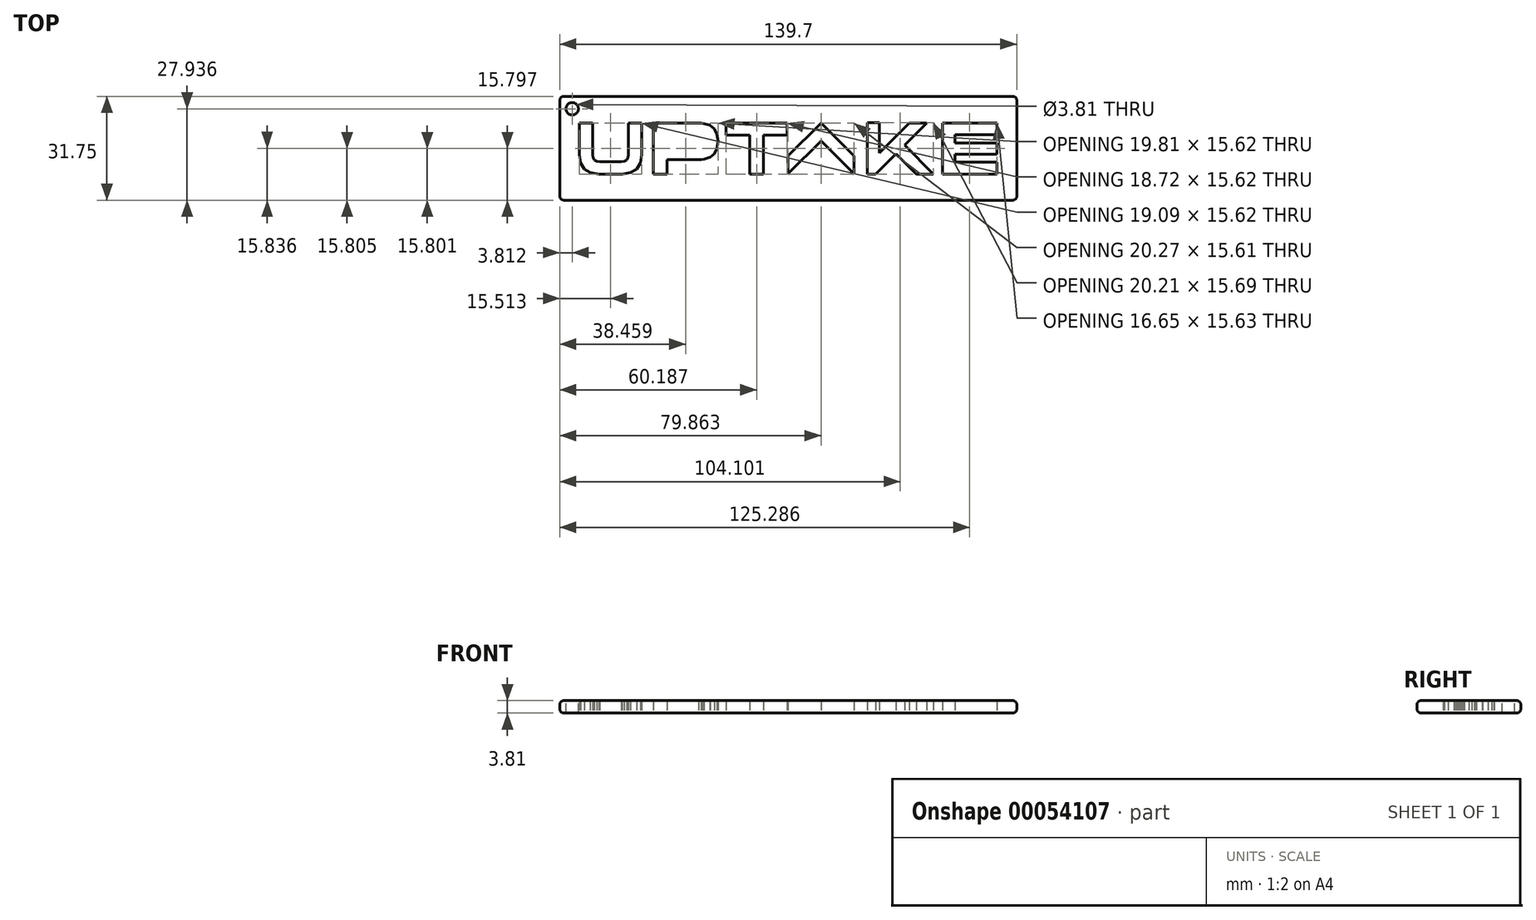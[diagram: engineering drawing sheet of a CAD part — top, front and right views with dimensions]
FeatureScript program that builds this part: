
annotation { "Feature Type Name" : "Feature", "Feature Type Description" : "" }
export const myFeature = defineFeature(function(context is Context, id is Id, definition is map)
    precondition{}
    {
        {
            var Q0;
            Q0=qCreatedBy(makeId("Top.planeOp"),FACE);
            var sketch = newSketch(context, id + "F0", { "sketchPlane" : qUnion([Q0])});
            skLineSegment(sketch, "E0", {"start": v(-25.67, 1.94) * mm, "end": v(-25.78, 1.11) * mm});
            skLineSegment(sketch, "E1", {"start": v(-25.78, 1.11) * mm, "end": v(-26.12, 0.53) * mm});
            skLineSegment(sketch, "E2", {"start": v(-26.12, 0.53) * mm, "end": v(-26.68, 0.18) * mm});
            skLineSegment(sketch, "E3", {"start": v(-26.68, 0.18) * mm, "end": v(-27.43, 0.05) * mm});
            skLineSegment(sketch, "E4", {"start": v(-27.43, 0.05) * mm, "end": v(-37.24, 0.05) * mm});
            skLineSegment(sketch, "E5", {"start": v(-37.24, 0.05) * mm, "end": v(-37.24, 4) * mm});
            skLineSegment(sketch, "E6", {"start": v(-37.24, 4) * mm, "end": v(-27.43, 4) * mm});
            skLineSegment(sketch, "E7", {"start": v(-27.43, 4) * mm, "end": v(-26.68, 3.88) * mm});
            skLineSegment(sketch, "E8", {"start": v(-26.68, 3.88) * mm, "end": v(-26.12, 3.53) * mm});
            skLineSegment(sketch, "E9", {"start": v(-26.12, 3.53) * mm, "end": v(-25.78, 2.94) * mm});
            skLineSegment(sketch, "E10", {"start": v(-25.78, 2.94) * mm, "end": v(-25.67, 2.12) * mm});
            skLineSegment(sketch, "E11", {"start": v(-25.67, 2.12) * mm, "end": v(-25.67, 1.94) * mm});
            skLineSegment(sketch, "E12", {"start": v(-26.08, 7.62) * mm, "end": v(-26.8, 7.7) * mm});
            skLineSegment(sketch, "E13", {"start": v(-26.8, 7.7) * mm, "end": v(-27.55, 7.73) * mm});
            skLineSegment(sketch, "E14", {"start": v(-27.55, 7.73) * mm, "end": v(-41.43, 7.73) * mm});
            skLineSegment(sketch, "E15", {"start": v(-41.43, 7.73) * mm, "end": v(-41.43, -7.9) * mm});
            skLineSegment(sketch, "E16", {"start": v(-41.43, -7.9) * mm, "end": v(-37.24, -7.9) * mm});
            skLineSegment(sketch, "E17", {"start": v(-37.24, -7.9) * mm, "end": v(-37.24, -3.54) * mm});
            skLineSegment(sketch, "E18", {"start": v(-37.24, -3.54) * mm, "end": v(-27.55, -3.54) * mm});
            skLineSegment(sketch, "E19", {"start": v(-27.55, -3.54) * mm, "end": v(-26.6, -3.5) * mm});
            skLineSegment(sketch, "E20", {"start": v(-26.6, -3.5) * mm, "end": v(-25.85, -3.4) * mm});
            skLineSegment(sketch, "E21", {"start": v(-25.85, -3.4) * mm, "end": v(-24.03, -2.78) * mm});
            skLineSegment(sketch, "E22", {"start": v(-24.03, -2.78) * mm, "end": v(-22.7, -1.66) * mm});
            skLineSegment(sketch, "E23", {"start": v(-22.7, -1.66) * mm, "end": v(-21.9, -0.03) * mm});
            skLineSegment(sketch, "E24", {"start": v(-21.9, -0.03) * mm, "end": v(-21.61, 2.07) * mm});
            skLineSegment(sketch, "E25", {"start": v(-21.61, 2.07) * mm, "end": v(-21.9, 4.23) * mm});
            skLineSegment(sketch, "E26", {"start": v(-21.9, 4.23) * mm, "end": v(-22.76, 5.9) * mm});
            skLineSegment(sketch, "E27", {"start": v(-22.76, 5.9) * mm, "end": v(-24.16, 7.03) * mm});
            skLineSegment(sketch, "E28", {"start": v(-24.16, 7.03) * mm, "end": v(-26.08, 7.62) * mm});
            skLineSegment(sketch, "E29", {"start": v(63.63, -7.9) * mm, "end": v(46.98, -7.9) * mm});
            skLineSegment(sketch, "E30", {"start": v(46.98, -7.9) * mm, "end": v(46.98, 7.73) * mm});
            skLineSegment(sketch, "E31", {"start": v(46.98, 7.73) * mm, "end": v(63.63, 7.73) * mm});
            skLineSegment(sketch, "E32", {"start": v(63.63, 7.73) * mm, "end": v(63.63, 4.11) * mm});
            skLineSegment(sketch, "E33", {"start": v(63.63, 4.11) * mm, "end": v(50.79, 4.11) * mm});
            skLineSegment(sketch, "E34", {"start": v(50.79, 4.11) * mm, "end": v(50.79, 1.6) * mm});
            skLineSegment(sketch, "E35", {"start": v(50.79, 1.6) * mm, "end": v(63.63, 1.6) * mm});
            skLineSegment(sketch, "E36", {"start": v(63.63, 1.6) * mm, "end": v(63.63, -1.8) * mm});
            skLineSegment(sketch, "E37", {"start": v(63.63, -1.8) * mm, "end": v(50.79, -1.8) * mm});
            skLineSegment(sketch, "E38", {"start": v(50.79, -1.8) * mm, "end": v(50.79, -4.28) * mm});
            skLineSegment(sketch, "E39", {"start": v(50.79, -4.28) * mm, "end": v(63.63, -4.28) * mm});
            skLineSegment(sketch, "E40", {"start": v(63.63, -4.28) * mm, "end": v(63.63, -7.9) * mm});
            skLineSegment(sketch, "E41", {"start": v(-11.89, -7.9) * mm, "end": v(-7.7, -7.9) * mm});
            skLineSegment(sketch, "E42", {"start": v(-7.7, -7.9) * mm, "end": v(-7.7, 4) * mm});
            skLineSegment(sketch, "E43", {"start": v(-7.7, 4) * mm, "end": v(-0.43, 4) * mm});
            skLineSegment(sketch, "E44", {"start": v(-0.43, 4) * mm, "end": v(-0.43, 7.73) * mm});
            skLineSegment(sketch, "E45", {"start": v(-0.43, 7.73) * mm, "end": v(-19.15, 7.73) * mm});
            skLineSegment(sketch, "E46", {"start": v(-19.15, 7.73) * mm, "end": v(-19.15, 4) * mm});
            skLineSegment(sketch, "E47", {"start": v(-19.15, 4) * mm, "end": v(-11.89, 4) * mm});
            skLineSegment(sketch, "E48", {"start": v(-11.89, 4) * mm, "end": v(-11.89, -7.9) * mm});
            skLineSegment(sketch, "E49", {"start": v(-58.08, -7.9) * mm, "end": v(-50.86, -7.9) * mm});
            skLineSegment(sketch, "E50", {"start": v(-50.86, -7.9) * mm, "end": v(-48.31, -7.49) * mm});
            skLineSegment(sketch, "E51", {"start": v(-48.31, -7.49) * mm, "end": v(-46.47, -6.35) * mm});
            skLineSegment(sketch, "E52", {"start": v(-46.47, -6.35) * mm, "end": v(-45.34, -4.5) * mm});
            skLineSegment(sketch, "E53", {"start": v(-45.34, -4.5) * mm, "end": v(-44.92, -1.95) * mm});
            skLineSegment(sketch, "E54", {"start": v(-44.92, -1.95) * mm, "end": v(-44.92, 7.73) * mm});
            skLineSegment(sketch, "E55", {"start": v(-44.92, 7.73) * mm, "end": v(-48.97, 7.73) * mm});
            skLineSegment(sketch, "E56", {"start": v(-48.97, 7.73) * mm, "end": v(-48.97, -1.95) * mm});
            skLineSegment(sketch, "E57", {"start": v(-48.97, -1.95) * mm, "end": v(-49.12, -2.88) * mm});
            skLineSegment(sketch, "E58", {"start": v(-49.12, -2.88) * mm, "end": v(-49.55, -3.56) * mm});
            skLineSegment(sketch, "E59", {"start": v(-49.55, -3.56) * mm, "end": v(-50.25, -3.99) * mm});
            skLineSegment(sketch, "E60", {"start": v(-50.25, -3.99) * mm, "end": v(-51.18, -4.16) * mm});
            skLineSegment(sketch, "E61", {"start": v(-51.18, -4.16) * mm, "end": v(-57.75, -4.16) * mm});
            skLineSegment(sketch, "E62", {"start": v(-57.75, -4.16) * mm, "end": v(-58.7, -3.98) * mm});
            skLineSegment(sketch, "E63", {"start": v(-58.7, -3.98) * mm, "end": v(-59.38, -3.57) * mm});
            skLineSegment(sketch, "E64", {"start": v(-59.38, -3.57) * mm, "end": v(-59.8, -2.9) * mm});
            skLineSegment(sketch, "E65", {"start": v(-59.8, -2.9) * mm, "end": v(-59.96, -1.95) * mm});
            skLineSegment(sketch, "E66", {"start": v(-59.96, -1.95) * mm, "end": v(-59.96, 7.73) * mm});
            skLineSegment(sketch, "E67", {"start": v(-59.96, 7.73) * mm, "end": v(-64.01, 7.73) * mm});
            skLineSegment(sketch, "E68", {"start": v(-64.01, 7.73) * mm, "end": v(-64.01, -1.95) * mm});
            skLineSegment(sketch, "E69", {"start": v(-64.01, -1.95) * mm, "end": v(-63.6, -4.5) * mm});
            skLineSegment(sketch, "E70", {"start": v(-63.6, -4.5) * mm, "end": v(-62.47, -6.35) * mm});
            skLineSegment(sketch, "E71", {"start": v(-62.47, -6.35) * mm, "end": v(-60.63, -7.49) * mm});
            skLineSegment(sketch, "E72", {"start": v(-60.63, -7.49) * mm, "end": v(-58.08, -7.9) * mm});
            skLineSegment(sketch, "E73", {"start": v(44.23, -7.9) * mm, "end": v(38.96, -7.9) * mm});
            skLineSegment(sketch, "E74", {"start": v(38.96, -7.9) * mm, "end": v(32.77, -1.7) * mm});
            skLineSegment(sketch, "E75", {"start": v(32.77, -1.7) * mm, "end": v(26.58, -7.9) * mm});
            skLineSegment(sketch, "E76", {"start": v(26.58, -7.9) * mm, "end": v(24.02, -7.9) * mm});
            skLineSegment(sketch, "E77", {"start": v(24.02, -7.9) * mm, "end": v(24.02, 7.8) * mm});
            skLineSegment(sketch, "E78", {"start": v(24.02, 7.8) * mm, "end": v(27.76, 7.8) * mm});
            skLineSegment(sketch, "E79", {"start": v(27.76, 7.8) * mm, "end": v(27.76, -1.44) * mm});
            skLineSegment(sketch, "E80", {"start": v(27.76, -1.44) * mm, "end": v(36.9, 7.73) * mm});
            skLineSegment(sketch, "E81", {"start": v(36.9, 7.73) * mm, "end": v(42.2, 7.73) * mm});
            skLineSegment(sketch, "E82", {"start": v(42.2, 7.73) * mm, "end": v(35.4, 0.93) * mm});
            skLineSegment(sketch, "E83", {"start": v(35.4, 0.93) * mm, "end": v(44.23, -7.9) * mm});
            skLineSegment(sketch, "E84", {"start": v(19.96, -2.35) * mm, "end": v(10.02, 7.6) * mm});
            skLineSegment(sketch, "E85", {"start": v(10.02, 7.6) * mm, "end": v(9.88, 7.73) * mm});
            skLineSegment(sketch, "E86", {"start": v(9.88, 7.73) * mm, "end": v(9.75, 7.6) * mm});
            skLineSegment(sketch, "E87", {"start": v(9.75, 7.6) * mm, "end": v(-0.2, -2.35) * mm});
            skLineSegment(sketch, "E88", {"start": v(-0.2, -2.35) * mm, "end": v(-0.25, -2.4) * mm});
            skLineSegment(sketch, "E89", {"start": v(-0.25, -2.4) * mm, "end": v(-0.25, -2.48) * mm});
            skLineSegment(sketch, "E90", {"start": v(-0.25, -2.48) * mm, "end": v(-0.25, -7.43) * mm});
            skLineSegment(sketch, "E91", {"start": v(-0.25, -7.43) * mm, "end": v(-0.25, -7.88) * mm});
            skLineSegment(sketch, "E92", {"start": v(-0.25, -7.88) * mm, "end": v(0.06, -7.56) * mm});
            skLineSegment(sketch, "E93", {"start": v(0.06, -7.56) * mm, "end": v(9.88, 2.25) * mm});
            skLineSegment(sketch, "E94", {"start": v(9.88, 2.25) * mm, "end": v(19.7, -7.56) * mm});
            skLineSegment(sketch, "E95", {"start": v(19.7, -7.56) * mm, "end": v(20.02, -7.88) * mm});
            skLineSegment(sketch, "E96", {"start": v(20.02, -7.88) * mm, "end": v(20.02, -7.43) * mm});
            skLineSegment(sketch, "E97", {"start": v(20.02, -7.43) * mm, "end": v(20.02, -2.48) * mm});
            skLineSegment(sketch, "E98", {"start": v(20.02, -2.48) * mm, "end": v(20.02, -2.4) * mm});
            skLineSegment(sketch, "E99", {"start": v(20.02, -2.4) * mm, "end": v(19.96, -2.35) * mm});
            skLineSegment(sketch, "E100.bottom", {"start": v(-69.98, 15.87) * mm, "end": v(69.72, 15.87) * mm});
            skLineSegment(sketch, "E100.top", {"start": v(-69.98, -15.88) * mm, "end": v(69.72, -15.88) * mm});
            skLineSegment(sketch, "E100.left", {"start": v(-69.98, 15.87) * mm, "end": v(-69.98, -15.88) * mm});
            skLineSegment(sketch, "E100.right", {"start": v(69.72, 15.87) * mm, "end": v(69.72, -15.88) * mm});
            skSolve(sketch);
        }
        {
            var Q0;
            Q0=makeQuery(id+"F0.imprint","IMPRINT",FACE,{"disambiguationData":[TD([[makeQuery(id+"F0.imprint","IMPRINT",EDGE,{"derivedFrom":sQuery(id+"F0.wireOp",EDGE,"E12")}),-1.0]])]});
            extrude(context, id + "F1", {"entities" : qUnion([Q0]), "depth" : 3.8 * mm});
        }
        {
            var Q0;
            Q0=makeQuery(id+"F1.opExtrude","CAP_FACE",FACE,{"disambiguationData":[OSD([sQuery(id+"F0.wireOp",EDGE,"E12"),sQuery(id+"F0.wireOp",EDGE,"E13"),sQuery(id+"F0.wireOp",EDGE,"E14"),sQuery(id+"F0.wireOp",EDGE,"E15"),sQuery(id+"F0.wireOp",EDGE,"E16"),sQuery(id+"F0.wireOp",EDGE,"E17"),sQuery(id+"F0.wireOp",EDGE,"E18"),sQuery(id+"F0.wireOp",EDGE,"E19"),sQuery(id+"F0.wireOp",EDGE,"E20"),sQuery(id+"F0.wireOp",EDGE,"E21"),sQuery(id+"F0.wireOp",EDGE,"E22"),sQuery(id+"F0.wireOp",EDGE,"E23"),sQuery(id+"F0.wireOp",EDGE,"E24"),sQuery(id+"F0.wireOp",EDGE,"E25"),sQuery(id+"F0.wireOp",EDGE,"E26"),sQuery(id+"F0.wireOp",EDGE,"E27"),sQuery(id+"F0.wireOp",EDGE,"E28"),sQuery(id+"F0.wireOp",EDGE,"E29"),sQuery(id+"F0.wireOp",EDGE,"E30"),sQuery(id+"F0.wireOp",EDGE,"E31"),sQuery(id+"F0.wireOp",EDGE,"E32"),sQuery(id+"F0.wireOp",EDGE,"E33"),sQuery(id+"F0.wireOp",EDGE,"E34"),sQuery(id+"F0.wireOp",EDGE,"E35"),sQuery(id+"F0.wireOp",EDGE,"E36"),sQuery(id+"F0.wireOp",EDGE,"E37"),sQuery(id+"F0.wireOp",EDGE,"E38"),sQuery(id+"F0.wireOp",EDGE,"E39"),sQuery(id+"F0.wireOp",EDGE,"E40"),sQuery(id+"F0.wireOp",EDGE,"E41"),sQuery(id+"F0.wireOp",EDGE,"E42"),sQuery(id+"F0.wireOp",EDGE,"E43"),sQuery(id+"F0.wireOp",EDGE,"E44"),sQuery(id+"F0.wireOp",EDGE,"E45"),sQuery(id+"F0.wireOp",EDGE,"E46"),sQuery(id+"F0.wireOp",EDGE,"E47"),sQuery(id+"F0.wireOp",EDGE,"E48"),sQuery(id+"F0.wireOp",EDGE,"E49"),sQuery(id+"F0.wireOp",EDGE,"E50"),sQuery(id+"F0.wireOp",EDGE,"E51"),sQuery(id+"F0.wireOp",EDGE,"E52"),sQuery(id+"F0.wireOp",EDGE,"E53"),sQuery(id+"F0.wireOp",EDGE,"E54"),sQuery(id+"F0.wireOp",EDGE,"E55"),sQuery(id+"F0.wireOp",EDGE,"E56"),sQuery(id+"F0.wireOp",EDGE,"E57"),sQuery(id+"F0.wireOp",EDGE,"E58"),sQuery(id+"F0.wireOp",EDGE,"E59"),sQuery(id+"F0.wireOp",EDGE,"E60"),sQuery(id+"F0.wireOp",EDGE,"E61"),sQuery(id+"F0.wireOp",EDGE,"E62"),sQuery(id+"F0.wireOp",EDGE,"E63"),sQuery(id+"F0.wireOp",EDGE,"E64"),sQuery(id+"F0.wireOp",EDGE,"E65"),sQuery(id+"F0.wireOp",EDGE,"E66"),sQuery(id+"F0.wireOp",EDGE,"E67"),sQuery(id+"F0.wireOp",EDGE,"E68"),sQuery(id+"F0.wireOp",EDGE,"E69"),sQuery(id+"F0.wireOp",EDGE,"E70"),sQuery(id+"F0.wireOp",EDGE,"E71"),sQuery(id+"F0.wireOp",EDGE,"E72"),sQuery(id+"F0.wireOp",EDGE,"E73"),sQuery(id+"F0.wireOp",EDGE,"E74"),sQuery(id+"F0.wireOp",EDGE,"E75"),sQuery(id+"F0.wireOp",EDGE,"E76"),sQuery(id+"F0.wireOp",EDGE,"E77"),sQuery(id+"F0.wireOp",EDGE,"E78"),sQuery(id+"F0.wireOp",EDGE,"E79"),sQuery(id+"F0.wireOp",EDGE,"E80"),sQuery(id+"F0.wireOp",EDGE,"E81"),sQuery(id+"F0.wireOp",EDGE,"E82"),sQuery(id+"F0.wireOp",EDGE,"E83"),sQuery(id+"F0.wireOp",EDGE,"E84"),sQuery(id+"F0.wireOp",EDGE,"E85"),sQuery(id+"F0.wireOp",EDGE,"E86"),sQuery(id+"F0.wireOp",EDGE,"E87"),sQuery(id+"F0.wireOp",EDGE,"E88"),sQuery(id+"F0.wireOp",EDGE,"E89"),sQuery(id+"F0.wireOp",EDGE,"E90"),sQuery(id+"F0.wireOp",EDGE,"E91"),sQuery(id+"F0.wireOp",EDGE,"E92"),sQuery(id+"F0.wireOp",EDGE,"E93"),sQuery(id+"F0.wireOp",EDGE,"E94"),sQuery(id+"F0.wireOp",EDGE,"E95"),sQuery(id+"F0.wireOp",EDGE,"E96"),sQuery(id+"F0.wireOp",EDGE,"E97"),sQuery(id+"F0.wireOp",EDGE,"E98"),sQuery(id+"F0.wireOp",EDGE,"E99"),sQuery(id+"F0.wireOp",EDGE,"E100.bottom"),sQuery(id+"F0.wireOp",EDGE,"E100.top"),sQuery(id+"F0.wireOp",EDGE,"E100.left"),sQuery(id+"F0.wireOp",EDGE,"E100.right")])],"isStart":false});
            var sketch = newSketch(context, id + "F2", { "sketchPlane" : qUnion([Q0])});
            skPoint(sketch, "E101", {"position": v(-66.17, 12.06) * mm});
            skSolve(sketch);
        }
        {
            var Q0;
            Q0=sQuery(id+"F2.wireOp",VERTEX,"E101");
            var Q1;
            Q1=makeQuery(id+"F1.opExtrude","SWEPT_BODY",BODY,{"disambiguationData":[OSD([sQuery(id+"F0.wireOp",EDGE,"E12"),sQuery(id+"F0.wireOp",EDGE,"E13"),sQuery(id+"F0.wireOp",EDGE,"E14"),sQuery(id+"F0.wireOp",EDGE,"E15"),sQuery(id+"F0.wireOp",EDGE,"E16"),sQuery(id+"F0.wireOp",EDGE,"E17"),sQuery(id+"F0.wireOp",EDGE,"E18"),sQuery(id+"F0.wireOp",EDGE,"E19"),sQuery(id+"F0.wireOp",EDGE,"E20"),sQuery(id+"F0.wireOp",EDGE,"E21"),sQuery(id+"F0.wireOp",EDGE,"E22"),sQuery(id+"F0.wireOp",EDGE,"E23"),sQuery(id+"F0.wireOp",EDGE,"E24"),sQuery(id+"F0.wireOp",EDGE,"E25"),sQuery(id+"F0.wireOp",EDGE,"E26"),sQuery(id+"F0.wireOp",EDGE,"E27"),sQuery(id+"F0.wireOp",EDGE,"E28"),sQuery(id+"F0.wireOp",EDGE,"E29"),sQuery(id+"F0.wireOp",EDGE,"E30"),sQuery(id+"F0.wireOp",EDGE,"E31"),sQuery(id+"F0.wireOp",EDGE,"E32"),sQuery(id+"F0.wireOp",EDGE,"E33"),sQuery(id+"F0.wireOp",EDGE,"E34"),sQuery(id+"F0.wireOp",EDGE,"E35"),sQuery(id+"F0.wireOp",EDGE,"E36"),sQuery(id+"F0.wireOp",EDGE,"E37"),sQuery(id+"F0.wireOp",EDGE,"E38"),sQuery(id+"F0.wireOp",EDGE,"E39"),sQuery(id+"F0.wireOp",EDGE,"E40"),sQuery(id+"F0.wireOp",EDGE,"E41"),sQuery(id+"F0.wireOp",EDGE,"E42"),sQuery(id+"F0.wireOp",EDGE,"E43"),sQuery(id+"F0.wireOp",EDGE,"E44"),sQuery(id+"F0.wireOp",EDGE,"E45"),sQuery(id+"F0.wireOp",EDGE,"E46"),sQuery(id+"F0.wireOp",EDGE,"E47"),sQuery(id+"F0.wireOp",EDGE,"E48"),sQuery(id+"F0.wireOp",EDGE,"E49"),sQuery(id+"F0.wireOp",EDGE,"E50"),sQuery(id+"F0.wireOp",EDGE,"E51"),sQuery(id+"F0.wireOp",EDGE,"E52"),sQuery(id+"F0.wireOp",EDGE,"E53"),sQuery(id+"F0.wireOp",EDGE,"E54"),sQuery(id+"F0.wireOp",EDGE,"E55"),sQuery(id+"F0.wireOp",EDGE,"E56"),sQuery(id+"F0.wireOp",EDGE,"E57"),sQuery(id+"F0.wireOp",EDGE,"E58"),sQuery(id+"F0.wireOp",EDGE,"E59"),sQuery(id+"F0.wireOp",EDGE,"E60"),sQuery(id+"F0.wireOp",EDGE,"E61"),sQuery(id+"F0.wireOp",EDGE,"E62"),sQuery(id+"F0.wireOp",EDGE,"E63"),sQuery(id+"F0.wireOp",EDGE,"E64"),sQuery(id+"F0.wireOp",EDGE,"E65"),sQuery(id+"F0.wireOp",EDGE,"E66"),sQuery(id+"F0.wireOp",EDGE,"E67"),sQuery(id+"F0.wireOp",EDGE,"E68"),sQuery(id+"F0.wireOp",EDGE,"E69"),sQuery(id+"F0.wireOp",EDGE,"E70"),sQuery(id+"F0.wireOp",EDGE,"E71"),sQuery(id+"F0.wireOp",EDGE,"E72"),sQuery(id+"F0.wireOp",EDGE,"E73"),sQuery(id+"F0.wireOp",EDGE,"E74"),sQuery(id+"F0.wireOp",EDGE,"E75"),sQuery(id+"F0.wireOp",EDGE,"E76"),sQuery(id+"F0.wireOp",EDGE,"E77"),sQuery(id+"F0.wireOp",EDGE,"E78"),sQuery(id+"F0.wireOp",EDGE,"E79"),sQuery(id+"F0.wireOp",EDGE,"E80"),sQuery(id+"F0.wireOp",EDGE,"E81"),sQuery(id+"F0.wireOp",EDGE,"E82"),sQuery(id+"F0.wireOp",EDGE,"E83"),sQuery(id+"F0.wireOp",EDGE,"E84"),sQuery(id+"F0.wireOp",EDGE,"E85"),sQuery(id+"F0.wireOp",EDGE,"E86"),sQuery(id+"F0.wireOp",EDGE,"E87"),sQuery(id+"F0.wireOp",EDGE,"E88"),sQuery(id+"F0.wireOp",EDGE,"E89"),sQuery(id+"F0.wireOp",EDGE,"E90"),sQuery(id+"F0.wireOp",EDGE,"E91"),sQuery(id+"F0.wireOp",EDGE,"E92"),sQuery(id+"F0.wireOp",EDGE,"E93"),sQuery(id+"F0.wireOp",EDGE,"E94"),sQuery(id+"F0.wireOp",EDGE,"E95"),sQuery(id+"F0.wireOp",EDGE,"E96"),sQuery(id+"F0.wireOp",EDGE,"E97"),sQuery(id+"F0.wireOp",EDGE,"E98"),sQuery(id+"F0.wireOp",EDGE,"E99"),sQuery(id+"F0.wireOp",EDGE,"E100.bottom"),sQuery(id+"F0.wireOp",EDGE,"E100.top"),sQuery(id+"F0.wireOp",EDGE,"E100.left"),sQuery(id+"F0.wireOp",EDGE,"E100.right")])]});
            hole(context, id + "F3", {"style" : HoleStyle.SIMPLE, "holeDiameter" : 3.8 * mm, "endStyle" : HoleEndStyle.THROUGH, "locations" : qUnion([Q0]), "scope" : qUnion([Q1])});
        }
        {
            var Q0;
            Q0=makeQuery(id+"F1.opExtrude","CAP_EDGE",EDGE,{"disambiguationData":[OSD([sQuery(id+"F0.wireOp",EDGE,"E100.bottom")])],"isStart":false});
            var Q1;
            Q1=makeQuery(id+"F1.opExtrude","CAP_EDGE",EDGE,{"disambiguationData":[OSD([sQuery(id+"F0.wireOp",EDGE,"E100.left")])],"isStart":false});
            var Q2;
            Q2=makeQuery(id+"F1.opExtrude","CAP_EDGE",EDGE,{"disambiguationData":[OSD([sQuery(id+"F0.wireOp",EDGE,"E100.top")])],"isStart":false});
            var Q3;
            Q3=makeQuery(id+"F1.opExtrude","CAP_EDGE",EDGE,{"disambiguationData":[OSD([sQuery(id+"F0.wireOp",EDGE,"E100.right")])],"isStart":false});
            var Q4;
            Q4=makeQuery(id+"F1.opExtrude","CAP_EDGE",EDGE,{"disambiguationData":[OSD([sQuery(id+"F0.wireOp",EDGE,"E100.right")])],"isStart":true});
            var Q5;
            Q5=makeQuery(id+"F1.opExtrude","CAP_EDGE",EDGE,{"disambiguationData":[OSD([sQuery(id+"F0.wireOp",EDGE,"E100.bottom")])],"isStart":true});
            var Q6;
            Q6=makeQuery(id+"F1.opExtrude","CAP_EDGE",EDGE,{"disambiguationData":[OSD([sQuery(id+"F0.wireOp",EDGE,"E100.top")])],"isStart":true});
            var Q7;
            Q7=makeQuery(id+"F1.opExtrude","CAP_EDGE",EDGE,{"disambiguationData":[OSD([sQuery(id+"F0.wireOp",EDGE,"E100.left")])],"isStart":true});
            var Q8;
            Q8=makeQuery(id+"F3.hole-0.boolean.opBoolean","COPY",EDGE,{"derivedFrom":makeQuery(id+"F3.hole-0.opRevolve","SWEPT_EDGE",EDGE,{"disambiguationData":[OSD([sQuery(id+"F3.hole-0.sketch.wireOp",EDGE,"core_line_2"),sQuery(id+"F3.hole-0.sketch.wireOp",EDGE,"core_line_3")])]})});
            var Q9;
            Q9=makeQuery(id+"F3.hole-0.boolean.opBoolean","INTERSECT",EDGE,{"derivedFrom":[makeQuery(id+"F1.opExtrude","CAP_FACE",FACE,{"disambiguationData":[OSD([sQuery(id+"F0.wireOp",EDGE,"E12"),sQuery(id+"F0.wireOp",EDGE,"E13"),sQuery(id+"F0.wireOp",EDGE,"E14"),sQuery(id+"F0.wireOp",EDGE,"E15"),sQuery(id+"F0.wireOp",EDGE,"E16"),sQuery(id+"F0.wireOp",EDGE,"E17"),sQuery(id+"F0.wireOp",EDGE,"E18"),sQuery(id+"F0.wireOp",EDGE,"E19"),sQuery(id+"F0.wireOp",EDGE,"E20"),sQuery(id+"F0.wireOp",EDGE,"E21"),sQuery(id+"F0.wireOp",EDGE,"E22"),sQuery(id+"F0.wireOp",EDGE,"E23"),sQuery(id+"F0.wireOp",EDGE,"E24"),sQuery(id+"F0.wireOp",EDGE,"E25"),sQuery(id+"F0.wireOp",EDGE,"E26"),sQuery(id+"F0.wireOp",EDGE,"E27"),sQuery(id+"F0.wireOp",EDGE,"E28"),sQuery(id+"F0.wireOp",EDGE,"E29"),sQuery(id+"F0.wireOp",EDGE,"E30"),sQuery(id+"F0.wireOp",EDGE,"E31"),sQuery(id+"F0.wireOp",EDGE,"E32"),sQuery(id+"F0.wireOp",EDGE,"E33"),sQuery(id+"F0.wireOp",EDGE,"E34"),sQuery(id+"F0.wireOp",EDGE,"E35"),sQuery(id+"F0.wireOp",EDGE,"E36"),sQuery(id+"F0.wireOp",EDGE,"E37"),sQuery(id+"F0.wireOp",EDGE,"E38"),sQuery(id+"F0.wireOp",EDGE,"E39"),sQuery(id+"F0.wireOp",EDGE,"E40"),sQuery(id+"F0.wireOp",EDGE,"E41"),sQuery(id+"F0.wireOp",EDGE,"E42"),sQuery(id+"F0.wireOp",EDGE,"E43"),sQuery(id+"F0.wireOp",EDGE,"E44"),sQuery(id+"F0.wireOp",EDGE,"E45"),sQuery(id+"F0.wireOp",EDGE,"E46"),sQuery(id+"F0.wireOp",EDGE,"E47"),sQuery(id+"F0.wireOp",EDGE,"E48"),sQuery(id+"F0.wireOp",EDGE,"E49"),sQuery(id+"F0.wireOp",EDGE,"E50"),sQuery(id+"F0.wireOp",EDGE,"E51"),sQuery(id+"F0.wireOp",EDGE,"E52"),sQuery(id+"F0.wireOp",EDGE,"E53"),sQuery(id+"F0.wireOp",EDGE,"E54"),sQuery(id+"F0.wireOp",EDGE,"E55"),sQuery(id+"F0.wireOp",EDGE,"E56"),sQuery(id+"F0.wireOp",EDGE,"E57"),sQuery(id+"F0.wireOp",EDGE,"E58"),sQuery(id+"F0.wireOp",EDGE,"E59"),sQuery(id+"F0.wireOp",EDGE,"E60"),sQuery(id+"F0.wireOp",EDGE,"E61"),sQuery(id+"F0.wireOp",EDGE,"E62"),sQuery(id+"F0.wireOp",EDGE,"E63"),sQuery(id+"F0.wireOp",EDGE,"E64"),sQuery(id+"F0.wireOp",EDGE,"E65"),sQuery(id+"F0.wireOp",EDGE,"E66"),sQuery(id+"F0.wireOp",EDGE,"E67"),sQuery(id+"F0.wireOp",EDGE,"E68"),sQuery(id+"F0.wireOp",EDGE,"E69"),sQuery(id+"F0.wireOp",EDGE,"E70"),sQuery(id+"F0.wireOp",EDGE,"E71"),sQuery(id+"F0.wireOp",EDGE,"E72"),sQuery(id+"F0.wireOp",EDGE,"E73"),sQuery(id+"F0.wireOp",EDGE,"E74"),sQuery(id+"F0.wireOp",EDGE,"E75"),sQuery(id+"F0.wireOp",EDGE,"E76"),sQuery(id+"F0.wireOp",EDGE,"E77"),sQuery(id+"F0.wireOp",EDGE,"E78"),sQuery(id+"F0.wireOp",EDGE,"E79"),sQuery(id+"F0.wireOp",EDGE,"E80"),sQuery(id+"F0.wireOp",EDGE,"E81"),sQuery(id+"F0.wireOp",EDGE,"E82"),sQuery(id+"F0.wireOp",EDGE,"E83"),sQuery(id+"F0.wireOp",EDGE,"E84"),sQuery(id+"F0.wireOp",EDGE,"E85"),sQuery(id+"F0.wireOp",EDGE,"E86"),sQuery(id+"F0.wireOp",EDGE,"E87"),sQuery(id+"F0.wireOp",EDGE,"E88"),sQuery(id+"F0.wireOp",EDGE,"E89"),sQuery(id+"F0.wireOp",EDGE,"E90"),sQuery(id+"F0.wireOp",EDGE,"E91"),sQuery(id+"F0.wireOp",EDGE,"E92"),sQuery(id+"F0.wireOp",EDGE,"E93"),sQuery(id+"F0.wireOp",EDGE,"E94"),sQuery(id+"F0.wireOp",EDGE,"E95"),sQuery(id+"F0.wireOp",EDGE,"E96"),sQuery(id+"F0.wireOp",EDGE,"E97"),sQuery(id+"F0.wireOp",EDGE,"E98"),sQuery(id+"F0.wireOp",EDGE,"E99"),sQuery(id+"F0.wireOp",EDGE,"E100.bottom"),sQuery(id+"F0.wireOp",EDGE,"E100.top"),sQuery(id+"F0.wireOp",EDGE,"E100.left"),sQuery(id+"F0.wireOp",EDGE,"E100.right")])],"isStart":true}),makeQuery(id+"F3.hole-0.opRevolve","SWEPT_FACE",FACE,{"disambiguationData":[OSD([sQuery(id+"F3.hole-0.sketch.wireOp",EDGE,"core_line_2")])]})]});
            var Q10;
            Q10=makeQuery(id+"F1.opExtrude","SWEPT_EDGE",EDGE,{"disambiguationData":[OSD([sQuery(id+"F0.wireOp",EDGE,"E100.bottom"),sQuery(id+"F0.wireOp",EDGE,"E100.left")])]});
            var Q11;
            Q11=makeQuery(id+"F1.opExtrude","SWEPT_EDGE",EDGE,{"disambiguationData":[OSD([sQuery(id+"F0.wireOp",EDGE,"E100.top"),sQuery(id+"F0.wireOp",EDGE,"E100.left")])]});
            var Q12;
            Q12=makeQuery(id+"F1.opExtrude","SWEPT_EDGE",EDGE,{"disambiguationData":[OSD([sQuery(id+"F0.wireOp",EDGE,"E100.top"),sQuery(id+"F0.wireOp",EDGE,"E100.right")])]});
            var Q13;
            Q13=makeQuery(id+"F1.opExtrude","SWEPT_EDGE",EDGE,{"disambiguationData":[OSD([sQuery(id+"F0.wireOp",EDGE,"E100.bottom"),sQuery(id+"F0.wireOp",EDGE,"E100.right")])]});
            fillet(context, id + "F4", {"entities" : qUnion([Q0, Q1, Q2, Q3, Q4, Q5, Q6, Q7, Q8, Q9, Q10, Q11, Q12, Q13]), "radius" : 1.27 * mm, "tangentPropagation" : true, "allowEdgeOverflow" : false});
        }
    });
